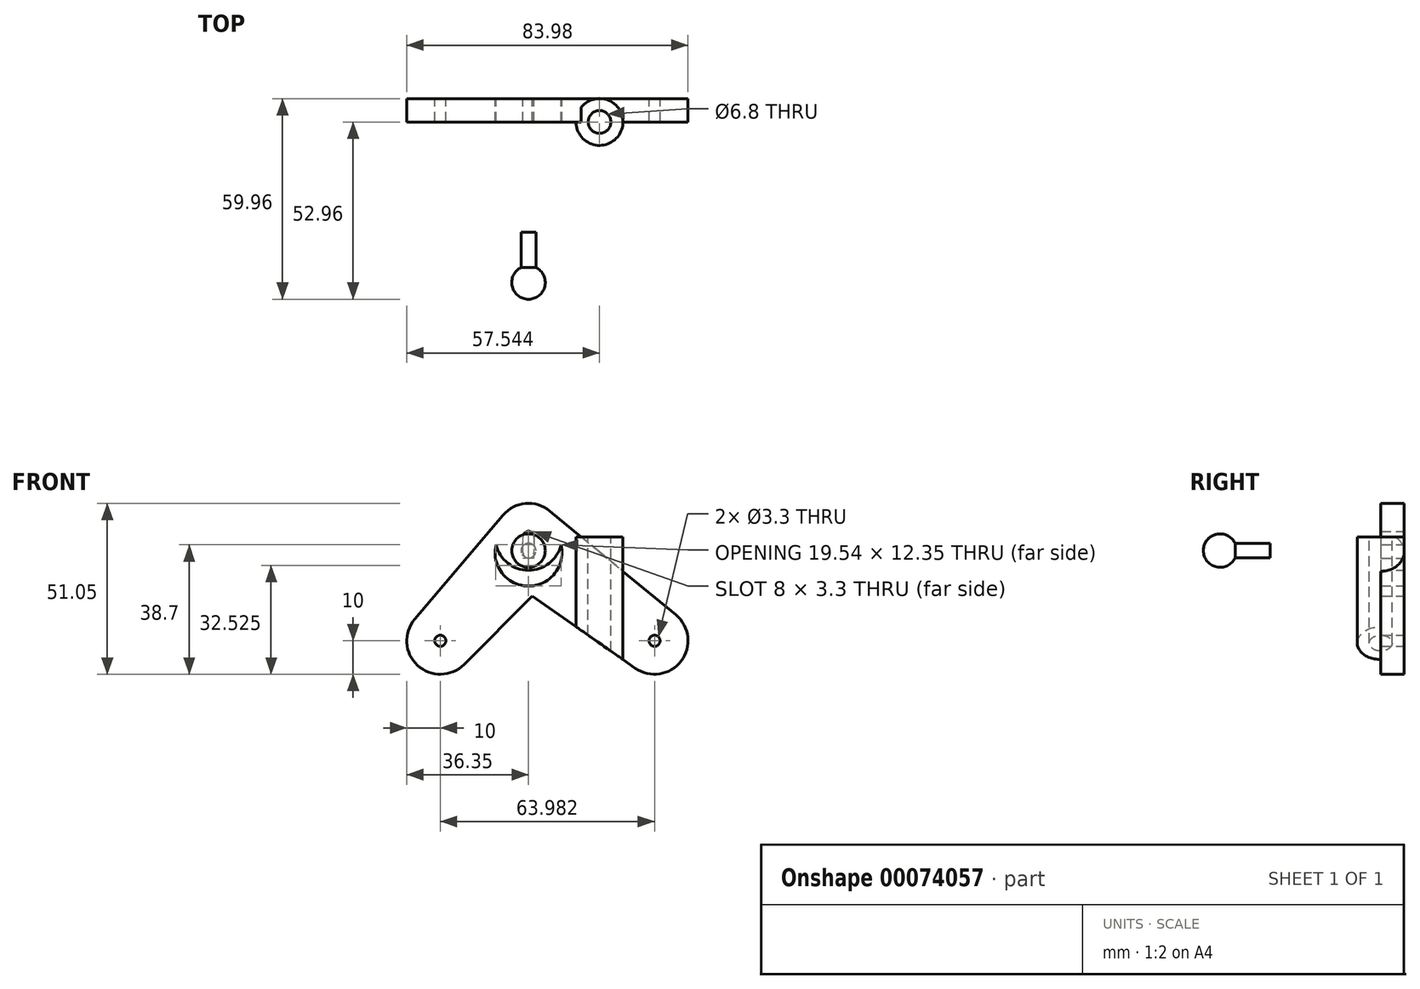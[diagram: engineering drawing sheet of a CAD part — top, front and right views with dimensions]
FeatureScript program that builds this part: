
annotation { "Feature Type Name" : "Feature", "Feature Type Description" : "" }
export const myFeature = defineFeature(function(context is Context, id is Id, definition is map)
    precondition{}
    {
        {
            var Q0;
            Q0=qCreatedBy(makeId("Front.planeOp"),FACE);
            var sketch = newSketch(context, id + "F0", { "sketchPlane" : qUnion([Q0])});
            skCircle(sketch, "E0", {"center": v(0, 0) * mm, "radius": 1.65 * mm});
            skCircle(sketch, "E1", {"center": v(0, -4.7) * mm, "radius": 1.65 * mm});
            skCircle(sketch, "E2", {"center": v(-26.35, -31.05) * mm, "radius": 1.65 * mm});
            skCircle(sketch, "E3", {"center": v(37.63, -31.05) * mm, "radius": 1.65 * mm});
            skLineSegment(sketch, "E4", {"start": v(1.65, 0) * mm, "end": v(1.65, -4.7) * mm});
            skLineSegment(sketch, "E5", {"start": v(-1.65, -4.7) * mm, "end": v(-1.65, 0) * mm});
            skLineSegment(sketch, "E6.bottom", {"start": v(81.04, -7) * mm, "end": v(-68.09, -7) * mm, "construction": true});
            skLineSegment(sketch, "E6.top", {"start": v(81.04, -26.05) * mm, "end": v(-68.09, -26.05) * mm, "construction": true});
            skLineSegment(sketch, "E6.left", {"start": v(81.04, -7) * mm, "end": v(81.04, -26.05) * mm, "construction": true});
            skLineSegment(sketch, "E6.right", {"start": v(-68.09, -7) * mm, "end": v(-68.09, -26.05) * mm, "construction": true});
            skCircle(sketch, "E7", {"center": v(-26.35, -31.05) * mm, "radius": 10 * mm});
            skCircle(sketch, "E8", {"center": v(37.63, -31.05) * mm, "radius": 10 * mm});
            skCircle(sketch, "E9", {"center": v(0, 0) * mm, "radius": 10 * mm});
            skCircle(sketch, "E10", {"center": v(0, -4.7) * mm, "radius": 10 * mm});
            skLineSegment(sketch, "E11", {"start": v(-26.35, -31.05) * mm, "end": v(0, -4.7) * mm, "construction": true});
            skLineSegment(sketch, "E12", {"start": v(37.63, -31.05) * mm, "end": v(0, -4.7) * mm, "construction": true});
            skLineSegment(sketch, "E13", {"start": v(44, -23.34) * mm, "end": v(6.36, 7.71) * mm});
            skLineSegment(sketch, "E14", {"start": v(-7.62, 6.47) * mm, "end": v(-33.97, -24.58) * mm});
            skLineSegment(sketch, "E15", {"start": v(-19.28, -38.12) * mm, "end": v(7.07, -11.77) * mm});
            skLineSegment(sketch, "E16", {"start": v(31.9, -39.24) * mm, "end": v(-5.74, -12.9) * mm});
            skCircle(sketch, "E17", {"center": v(0, 0) * mm, "radius": 5 * mm, "construction": true});
            skCircle(sketch, "E18", {"center": v(-26.35, -31.05) * mm, "radius": 5 * mm, "construction": true});
            skSolve(sketch);
        }
        {
            var Q0;
            Q0 = qSketchRegion(id + "F0", true);
            var Q1;
            {var subQ5=sQuery(id+"F0.wireOp",EDGE,"E4");Q1=makeQuery(id+"F0.imprint","IMPRINT",FACE,{"disambiguationData":[TD([[makeQuery(id+"F0.imprint","IMPRINT",EDGE,{"derivedFrom":subQ5}),1.0]])]});}
            var Q2;
            {var subQ0=sQuery(id+"F0.wireOp",EDGE,"E10");var subQ1=sQuery(id+"F0.wireOp",EDGE,"E9");var subQ2=makeQuery(id+"F0.imprint","INTERSECT",VERTEX,{"disambiguationData":[OD(0.0)],"derivedFrom":[subQ1,subQ0]});Q2=makeQuery(id+"F0.imprint","IMPRINT",FACE,{"disambiguationData":[TD([[makeQuery(id+"F0.imprint","IMPRINT",EDGE,{"disambiguationData":[TD([[subQ2,-1.0]])],"derivedFrom":subQ1}),-1.0]])]});}
            extrude(context, id + "F1", {"entities" : qUnion([Q0, Q1, Q2]), "depth" : 7 * mm});
        }
        {
            var Q0;
            Q0=qCreatedBy(makeId("Right.planeOp"),FACE);
            var sketch = newSketch(context, id + "F2", { "sketchPlane" : qUnion([Q0])});
            skLineSegment(sketch, "E19", {"start": v(-59.96, -4.11) * mm, "end": v(-39.96, -4.11) * mm, "construction": true});
            skArc(sketch, "E20", {"start": v(-50.47, -1.91) * mm, "mid": v(-56.1, 0.76) * mm, "end": v(-59.96, -4.11) * mm});
            skLineSegment(sketch, "E21", {"start": v(-50.47, -1.91) * mm, "end": v(-39.96, -1.91) * mm});
            skLineSegment(sketch, "E22", {"start": v(-39.96, -1.91) * mm, "end": v(-39.96, -4.11) * mm});
            skLineSegment(sketch, "E23", {"start": v(-59.96, -4.11) * mm, "end": v(-39.96, -4.11) * mm});
            skSolve(sketch);
        }
        {
            var Q0;
            Q0 = qSketchRegion(id + "F2", true);
            var Q1;
            Q1=sQuery(id+"F2.wireOp",EDGE,"E23");
            revolve(context, id + "F3", {"entities" : qUnion([Q0]), "axis" : qUnion([Q1]), "revolveType" : RevolveType.FULL});
        }
        {
            var Q0;
            Q0=qCreatedBy(makeId("Top.planeOp"),FACE);
            var sketch = newSketch(context, id + "F4", { "sketchPlane" : qUnion([Q0])});
            skCircle(sketch, "E24", {"center": v(21.2, -7) * mm, "radius": 3.4 * mm});
            skLineSegment(sketch, "E25.0", {"start": v(31.9, -7) * mm, "end": v(1.14, -7) * mm, "construction": true});
            skCircle(sketch, "E26", {"center": v(21.2, -7) * mm, "radius": 7 * mm});
            skSolve(sketch);
        }
        {
            var Q0;
            Q0 = qSketchRegion(id + "F4", true);
            var Q1;
            Q1=makeQuery(id+"F1.opExtrude","SWEPT_FACE",FACE,{"disambiguationData":[OSD([sQuery(id+"F0.wireOp",EDGE,"E16")])]});
            extrude(context, id + "F5", {"entities" : qUnion([Q0]), "operationType" : NewBodyOperationType.ADD, "endBound" : BoundingType.UP_TO_SURFACE, "oppositeDirection" : true, "endBoundEntityFace" : qUnion([Q1]), "depth" : 25 * mm});
        }
        {
            var Q0;
            Q0=makeQuery(id+"F4.imprint","IMPRINT",FACE,{"disambiguationData":[TD([[makeQuery(id+"F4.imprint","IMPRINT",EDGE,{"derivedFrom":sQuery(id+"F4.wireOp",EDGE,"E24")}),1.0]])]});
            extrude(context, id + "F6", {"entities" : qUnion([Q0]), "operationType" : NewBodyOperationType.REMOVE, "endBound" : BoundingType.THROUGH_ALL, "oppositeDirection" : true, "depth" : 25 * mm});
        }
    });
